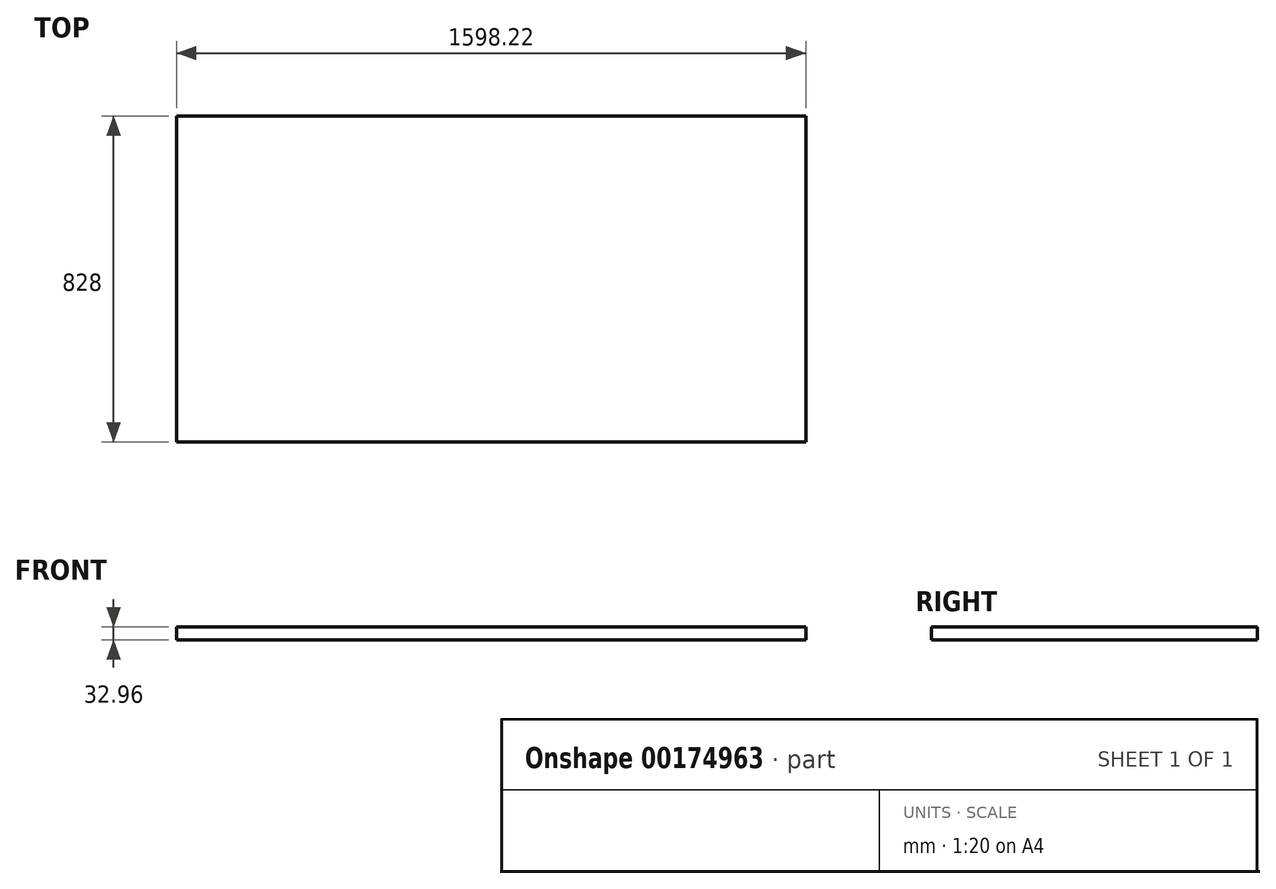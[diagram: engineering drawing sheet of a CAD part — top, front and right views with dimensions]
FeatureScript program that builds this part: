
annotation { "Feature Type Name" : "Feature", "Feature Type Description" : "" }
export const myFeature = defineFeature(function(context is Context, id is Id, definition is map)
    precondition{}
    {
        {
            var Q0;
            Q0=qCreatedBy(makeId("Top.planeOp"),FACE);
            var sketch = newSketch(context, id + "F0", { "sketchPlane" : qUnion([Q0])});
            skLineSegment(sketch, "E0.bottom", {"start": v(-799.11, 414) * mm, "end": v(799.11, 414) * mm});
            skLineSegment(sketch, "E0.top", {"start": v(-799.11, -414) * mm, "end": v(799.11, -414) * mm});
            skLineSegment(sketch, "E0.left", {"start": v(-799.11, 414) * mm, "end": v(-799.11, -414) * mm});
            skLineSegment(sketch, "E0.right", {"start": v(799.11, 414) * mm, "end": v(799.11, -414) * mm});
            skSolve(sketch);
        }
        {
            var Q0;
            Q0 = qSketchRegion(id + "F0", true);
            extrude(context, id + "F1", {"entities" : qUnion([Q0]), "depth" : 32.96 * mm});
        }
        {
            var Q0;
            Q0=makeQuery(id+"F1.opExtrude","SWEPT_FACE",FACE,{"disambiguationData":[OSD([sQuery(id+"F0.wireOp",EDGE,"E0.right")])]});
            var sketch = newSketch(context, id + "F2", { "sketchPlane" : qUnion([Q0])});
            skLineSegment(sketch, "E1.0", {"start": v(414, 0) * mm, "end": v(-414, 0) * mm});
            skLineSegment(sketch, "E2.0", {"start": v(414, 32.96) * mm, "end": v(-414, 32.96) * mm});
            skLineSegment(sketch, "E3.bottom", {"start": v(-301.56, 0) * mm, "end": v(338.9, 0) * mm});
            skLineSegment(sketch, "E3.top", {"start": v(-301.56, 18.8) * mm, "end": v(338.9, 18.8) * mm});
            skLineSegment(sketch, "E3.left", {"start": v(-301.56, 0) * mm, "end": v(-301.56, 18.8) * mm});
            skLineSegment(sketch, "E3.right", {"start": v(338.9, 0) * mm, "end": v(338.9, 18.8) * mm});
            skSolve(sketch);
        }
    });
